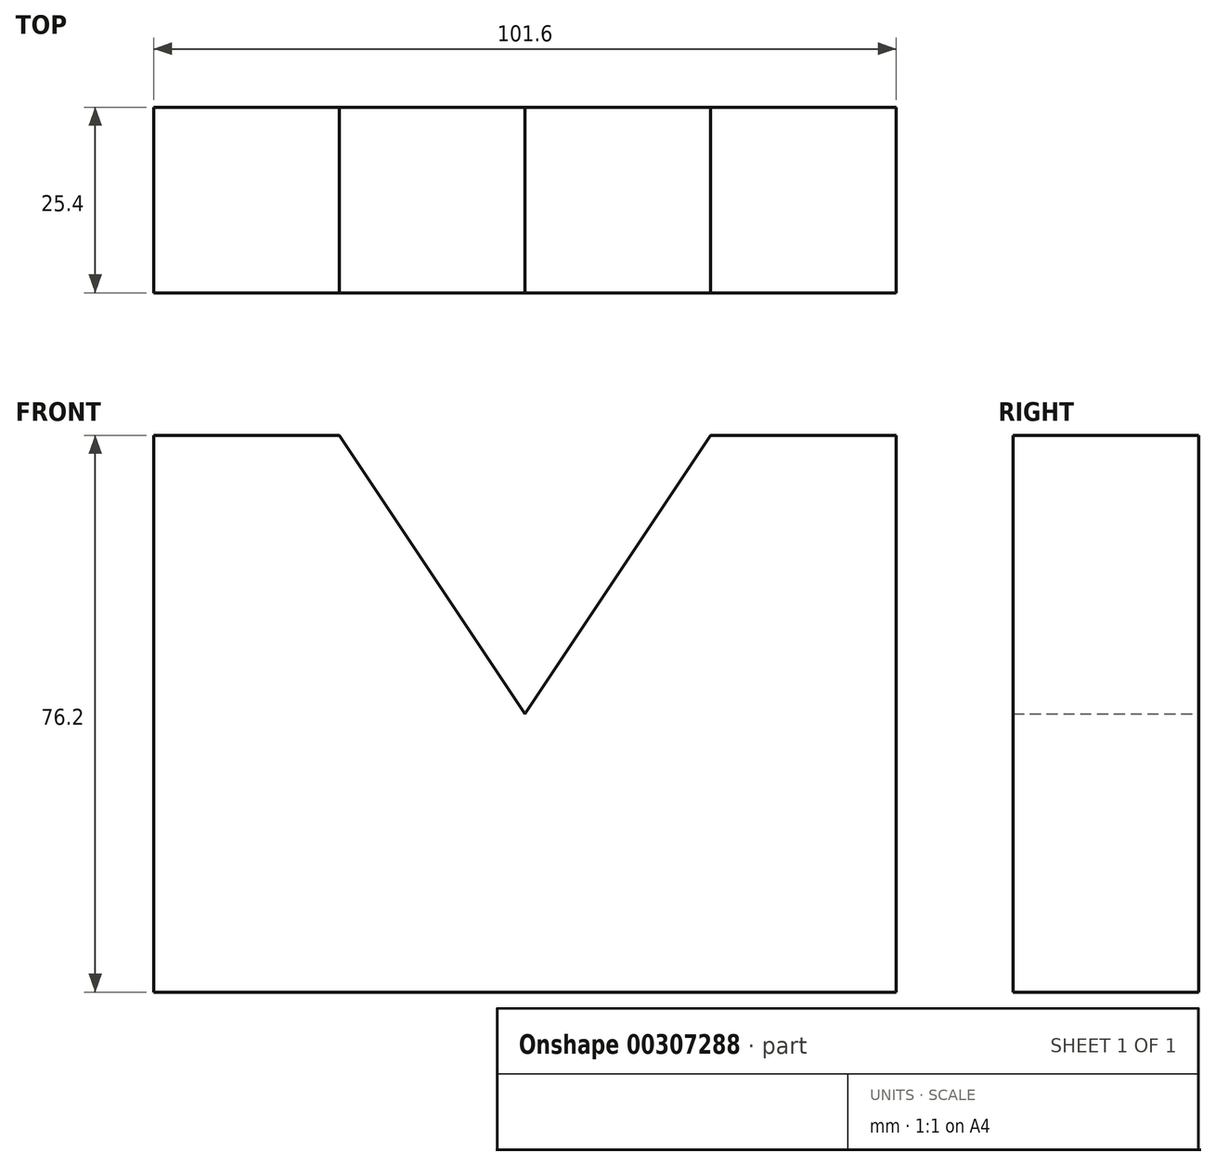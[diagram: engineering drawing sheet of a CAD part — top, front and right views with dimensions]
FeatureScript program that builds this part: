
annotation { "Feature Type Name" : "Feature", "Feature Type Description" : "" }
export const myFeature = defineFeature(function(context is Context, id is Id, definition is map)
    precondition{}
    {
        {
            var Q0;
            Q0=qCreatedBy(makeId("Front.planeOp"),FACE);
            var sketch = newSketch(context, id + "F0", { "sketchPlane" : qUnion([Q0])});
            skLineSegment(sketch, "E0", {"start": v(-52.62, -45.41) * mm, "end": v(48.98, -45.41) * mm});
            skLineSegment(sketch, "E1", {"start": v(48.98, -45.41) * mm, "end": v(48.98, 30.79) * mm});
            skLineSegment(sketch, "E2", {"start": v(48.98, 30.79) * mm, "end": v(23.58, 30.79) * mm});
            skLineSegment(sketch, "E3", {"start": v(-52.62, -45.41) * mm, "end": v(-52.62, 30.79) * mm});
            skLineSegment(sketch, "E4", {"start": v(-52.62, 30.79) * mm, "end": v(-27.22, 30.79) * mm});
            skPoint(sketch, "E5", {"position": v(-1.82, -7.31) * mm});
            skPoint(sketch, "E5.positionSnap0", {"position": v(-52.62, -7.31) * mm});
            skPoint(sketch, "E5.positionSnap1", {"position": v(-1.82, -45.41) * mm});
            skLineSegment(sketch, "E6", {"start": v(-27.22, 30.79) * mm, "end": v(-1.82, -7.31) * mm});
            skLineSegment(sketch, "E7", {"start": v(23.58, 30.79) * mm, "end": v(-1.82, -7.31) * mm});
            skSolve(sketch);
        }
        {
            var Q0;
            Q0=makeQuery(id+"F0.imprint","IMPRINT",FACE,{"disambiguationData":[TD([[makeQuery(id+"F0.imprint","IMPRINT",EDGE,{"derivedFrom":sQuery(id+"F0.wireOp",EDGE,"E0")}),1.0]])]});
            extrude(context, id + "F1", {"entities" : qUnion([Q0]), "depth" : 25.4 * mm});
        }
    });
